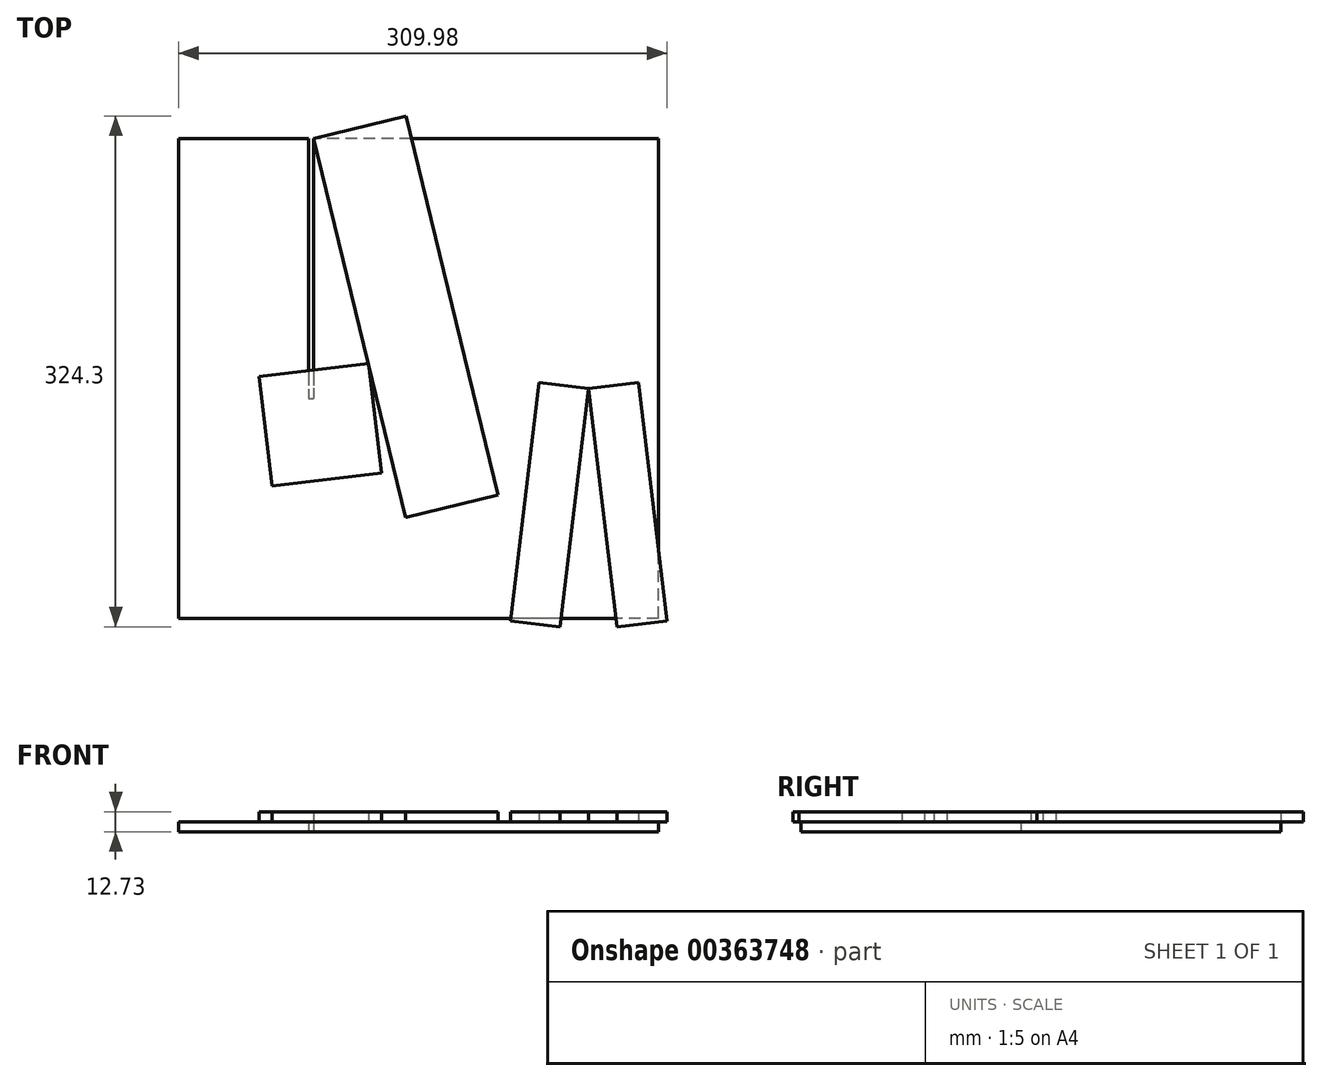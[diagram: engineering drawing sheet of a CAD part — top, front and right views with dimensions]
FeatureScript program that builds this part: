
annotation { "Feature Type Name" : "Feature", "Feature Type Description" : "" }
export const myFeature = defineFeature(function(context is Context, id is Id, definition is map)
    precondition{}
    {
        {
            var Q0;
            Q0=qCreatedBy(makeId("Top.planeOp"),FACE);
            var sketch = newSketch(context, id + "F0", { "sketchPlane" : qUnion([Q0])});
            skLineSegment(sketch, "E0.bottom", {"start": v(152.4, -152.4) * mm, "end": v(-152.4, -152.4) * mm});
            skLineSegment(sketch, "E0.top", {"start": v(152.4, 152.4) * mm, "end": v(-152.4, 152.4) * mm});
            skLineSegment(sketch, "E0.left", {"start": v(152.4, -152.4) * mm, "end": v(152.4, 152.4) * mm});
            skLineSegment(sketch, "E0.right", {"start": v(-152.4, -152.4) * mm, "end": v(-152.4, 152.4) * mm});
            skPoint(sketch, "E0.middle", {"position": v(0, 0) * mm});
            skLineSegment(sketch, "E1.bottom", {"start": v(-69.85, 152.4) * mm, "end": v(-66.68, 152.4) * mm});
            skLineSegment(sketch, "E1.top", {"start": v(-69.85, -12.7) * mm, "end": v(-66.67, -12.7) * mm});
            skLineSegment(sketch, "E1.left", {"start": v(-69.85, 152.4) * mm, "end": v(-69.85, -12.7) * mm});
            skLineSegment(sketch, "E1.right", {"start": v(-66.68, 152.4) * mm, "end": v(-66.67, -12.7) * mm});
            skSolve(sketch);
        }
        {
            var Q0;
            Q0=makeQuery(id+"F0.imprint","IMPRINT",FACE,{"disambiguationData":[TD([[makeQuery(id+"F0.imprint","IMPRINT",EDGE,{"derivedFrom":sQuery(id+"F0.wireOp",EDGE,"E0.bottom")}),-1.0]])]});
            extrude(context, id + "F1", {"entities" : qUnion([Q0]), "depth" : 6.35 * mm});
        }
        {
            var Q0;
            Q0=makeQuery(id+"F1.opExtrude","CAP_FACE",FACE,{"disambiguationData":[OSD([sQuery(id+"F0.wireOp",EDGE,"E0.bottom"),sQuery(id+"F0.wireOp",EDGE,"E0.top"),sQuery(id+"F0.wireOp",EDGE,"E0.left"),sQuery(id+"F0.wireOp",EDGE,"E0.right"),sQuery(id+"F0.wireOp",EDGE,"E1.top"),sQuery(id+"F0.wireOp",EDGE,"E1.left"),sQuery(id+"F0.wireOp",EDGE,"E1.right")])],"isStart":false});
            cPlane(context, id + "F2", {"entities" : qUnion([Q0]), "cplaneType" : CPlaneType.OFFSET, "offset" : 0.03 * mm, "width" : 152.4 * mm, "height" : 152.4 * mm});
        }
        {
            var Q0;
            Q0=qCreatedBy(id+"F2.planeOp",FACE);
            var sketch = newSketch(context, id + "F3", { "sketchPlane" : qUnion([Q0])});
            skLineSegment(sketch, "E2", {"start": v(-66.68, 152.4) * mm, "end": v(-66.67, 5.3) * mm});
            skLineSegment(sketch, "E3", {"start": v(-66.68, 152.4) * mm, "end": v(-31.98, 9.46) * mm});
            skLineSegment(sketch, "E4", {"start": v(-31.98, 9.46) * mm, "end": v(-66.67, 5.3) * mm});
            skLineSegment(sketch, "E5", {"start": v(-66.68, 152.4) * mm, "end": v(-49.33, 7.38) * mm});
            skSolve(sketch);
        }
        {
            var Q0;
            Q0=qCreatedBy(id+"F2.planeOp",FACE);
            var sketch = newSketch(context, id + "F4", { "sketchPlane" : qUnion([Q0])});
            skLineSegment(sketch, "E6.0", {"start": v(-66.68, 152.4) * mm, "end": v(-31.98, 9.46) * mm});
            skLineSegment(sketch, "E7", {"start": v(-66.68, 152.4) * mm, "end": v(-8.26, -88.26) * mm});
            skLineSegment(sketch, "E8", {"start": v(-8.26, -88.26) * mm, "end": v(50.37, -74.03) * mm});
            skLineSegment(sketch, "E9", {"start": v(50.37, -74.03) * mm, "end": v(-8.05, 166.63) * mm});
            skLineSegment(sketch, "E10", {"start": v(-66.68, 152.4) * mm, "end": v(-8.05, 166.63) * mm});
            skSolve(sketch);
        }
        {
            var Q0;
            Q0 = qSketchRegion(id + "F4", true);
            extrude(context, id + "F5", {"entities" : qUnion([Q0]), "depth" : 6.35 * mm});
        }
        {
            var Q0;
            Q0=qCreatedBy(id+"F2.planeOp",FACE);
            var sketch = newSketch(context, id + "F6", { "sketchPlane" : qUnion([Q0])});
            skLineSegment(sketch, "E11.0", {"start": v(-31.98, 9.46) * mm, "end": v(-66.67, 5.3) * mm});
            skLineSegment(sketch, "E12", {"start": v(-66.67, 5.3) * mm, "end": v(-101.33, 1.16) * mm});
            skLineSegment(sketch, "E13", {"start": v(-101.33, 1.16) * mm, "end": v(-93.04, -68.2) * mm});
            skLineSegment(sketch, "E14", {"start": v(-93.04, -68.2) * mm, "end": v(-23.68, -59.9) * mm});
            skLineSegment(sketch, "E15", {"start": v(-31.98, 9.46) * mm, "end": v(-23.68, -59.9) * mm});
            skSolve(sketch);
        }
        {
            var Q0;
            Q0 = qSketchRegion(id + "F6", true);
            extrude(context, id + "F7", {"entities" : qUnion([Q0]), "depth" : 6.35 * mm});
        }
        {
            var Q0;
            Q0=qCreatedBy(id+"F2.planeOp",FACE);
            var sketch = newSketch(context, id + "F8", { "sketchPlane" : qUnion([Q0])});
            skLineSegment(sketch, "E16", {"start": v(125.42, -152.4) * mm, "end": v(90.48, -152.4) * mm, "construction": true});
            skLineSegment(sketch, "E17", {"start": v(107.95, -152.4) * mm, "end": v(107.95, -6.35) * mm, "construction": true});
            skLineSegment(sketch, "E18", {"start": v(90.48, -152.4) * mm, "end": v(107.95, -6.35) * mm, "construction": true});
            skLineSegment(sketch, "E19", {"start": v(125.42, -152.4) * mm, "end": v(107.95, -6.35) * mm, "construction": true});
            skLineSegment(sketch, "E20", {"start": v(107.95, -6.35) * mm, "end": v(126.05, -157.67) * mm});
            skLineSegment(sketch, "E21", {"start": v(126.05, -157.67) * mm, "end": v(157.58, -153.9) * mm});
            skLineSegment(sketch, "E22", {"start": v(157.58, -153.9) * mm, "end": v(139.48, -2.58) * mm});
            skLineSegment(sketch, "E23", {"start": v(107.95, -6.35) * mm, "end": v(139.48, -2.58) * mm});
            skLineSegment(sketch, "E24.MirrorCS", {"start": v(58.32, -153.9) * mm, "end": v(76.42, -2.58) * mm});
            skLineSegment(sketch, "E25.MirrorCS", {"start": v(89.85, -157.67) * mm, "end": v(58.32, -153.9) * mm});
            skLineSegment(sketch, "E26.MirrorCS", {"start": v(107.95, -6.35) * mm, "end": v(76.42, -2.58) * mm});
            skLineSegment(sketch, "E27.MirrorCS", {"start": v(107.95, -6.35) * mm, "end": v(89.85, -157.67) * mm});
            skSolve(sketch);
        }
        {
            var Q0;
            Q0 = qSketchRegion(id + "F8", true);
            extrude(context, id + "F9", {"entities" : qUnion([Q0]), "depth" : 6.35 * mm});
        }
    });
